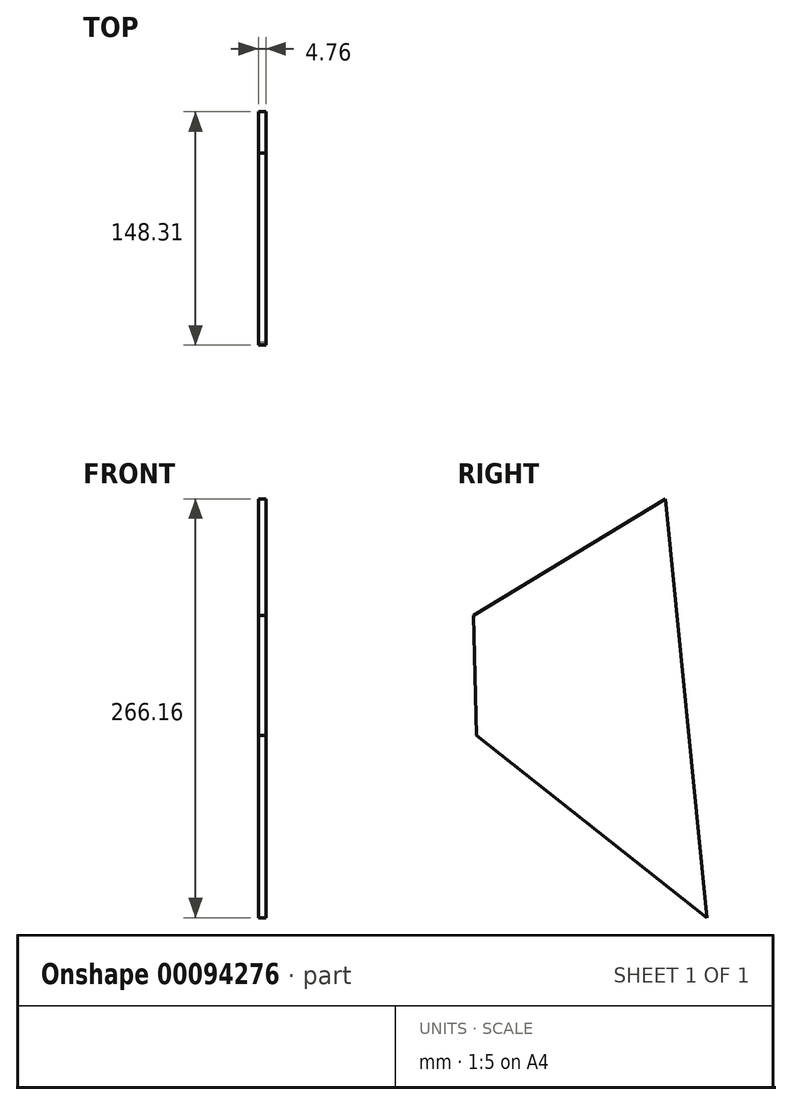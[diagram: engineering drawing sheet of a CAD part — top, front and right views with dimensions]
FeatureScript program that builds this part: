
annotation { "Feature Type Name" : "Feature", "Feature Type Description" : "" }
export const myFeature = defineFeature(function(context is Context, id is Id, definition is map)
    precondition{}
    {
        {
            var Q0;
            Q0=qCreatedBy(makeId("Right.planeOp"),FACE);
            var sketch = newSketch(context, id + "F0", { "sketchPlane" : qUnion([Q0])});
            skLineSegment(sketch, "E0", {"start": v(-121.9, 13.4) * mm, "end": v(0, 87.67) * mm});
            skLineSegment(sketch, "E1", {"start": v(0, 87.67) * mm, "end": v(26.4, -178.49) * mm});
            skLineSegment(sketch, "E2", {"start": v(-120.11, -62.78) * mm, "end": v(26.4, -178.49) * mm});
            skLineSegment(sketch, "E3", {"start": v(-121.9, 13.4) * mm, "end": v(-120.11, -62.78) * mm});
            skSolve(sketch);
        }
        {
            var Q0;
            Q0 = qSketchRegion(id + "F0", true);
            extrude(context, id + "F1", {"entities" : qUnion([Q0]), "depth" : 4.76 * mm});
        }
    });
